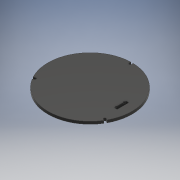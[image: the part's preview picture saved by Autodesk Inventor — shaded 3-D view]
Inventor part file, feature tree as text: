
AUTODESK INVENTOR PART (.ipt)
format: ipt  version: 2017 (Build 210142000, 142)  size: 173,568 bytes
history: native  units: mm
features: extrude x5, sketch x5, projected_geometry x3
ambient origin geometry x8: Origin, YZ Plane, XZ Plane, XY Plane, X Axis, Y Axis, Z Axis, Center Point
bodies: Solid1 (feature_tree)
feature tree (13):
  extrude  "Extrusion1"  Depth=2.0mm TaperAngle=0.0deg
  extrude  "Extrusion2"  Depth=1.8mm
  extrude  "Extrusion3"  Depth=2.0mm TaperAngle=0.0deg
  extrude  "Extrusion4"  Depth=9.0mm
  extrude  "Extrusion5"  Depth=3.0mm
  sketch  "Sketch1"  dims[d0=64.0mm d1=2.0mm d2=0.0mm]
  sketch  "Sketch2"  dims[d3=30.658mm d4=1.8mm]
  projected_geometry  "Projected Loop1"
  sketch  "Sketch3"  dims[d5=30.0mm d7=360.0deg d9=2.0mm d10=0.0mm]
  sketch  "Sketch4"  dims[d11=2.2mm d12=9.0mm]
  projected_geometry  "Projected Loop2"
  sketch  "Sketch5"  dims[d13=2.0mm d14=0.0mm d15=3.0mm d16=3.0mm d17=1.0mm d18=1.0mm d19=1.0mm d20=0.0mm d21=57.63mm d22=24.0mm d23=2.0mm d24=57.63mm d25=2.0mm d26=0.0mm]
  projected_geometry  "Projected Loop3"
